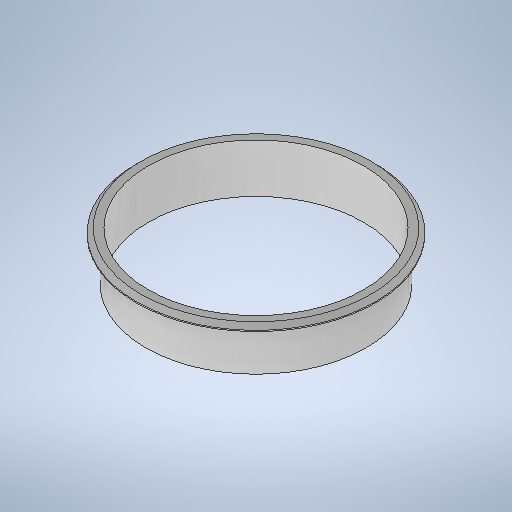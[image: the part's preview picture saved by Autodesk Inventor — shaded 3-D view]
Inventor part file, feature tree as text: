
AUTODESK INVENTOR PART (.ipt)
format: ipt  version: 2025.1 (Build 291241020, 241B)  size: 401,408 bytes
history: native  units: in
note: dims shown in document units (in); Inventor stores cm internally (conversion verified against a paired STEP export)
features: extrude x2, sketch x1, chamfer x1
ambient origin geometry x8: Origin, YZ Plane, XZ Plane, XY Plane, X Axis, Y Axis, Z Axis, Center Point
bodies: Solid1 (feature_tree)
feature tree (4):
  sketch  "Sketch1"  dims[d0=4.95in d1=5.5in d2=0.0625in d3=1.125in d4=0.0in d5=0.125in d6=0.0in d7=0.1in d8=0.125in d9=45.0deg]
  extrude  "Extrusion1"  Depth=0.125in
  extrude  "Extrusion2"  Depth=0.125in
  chamfer  "Chamfer1"  Distance=1.125in
